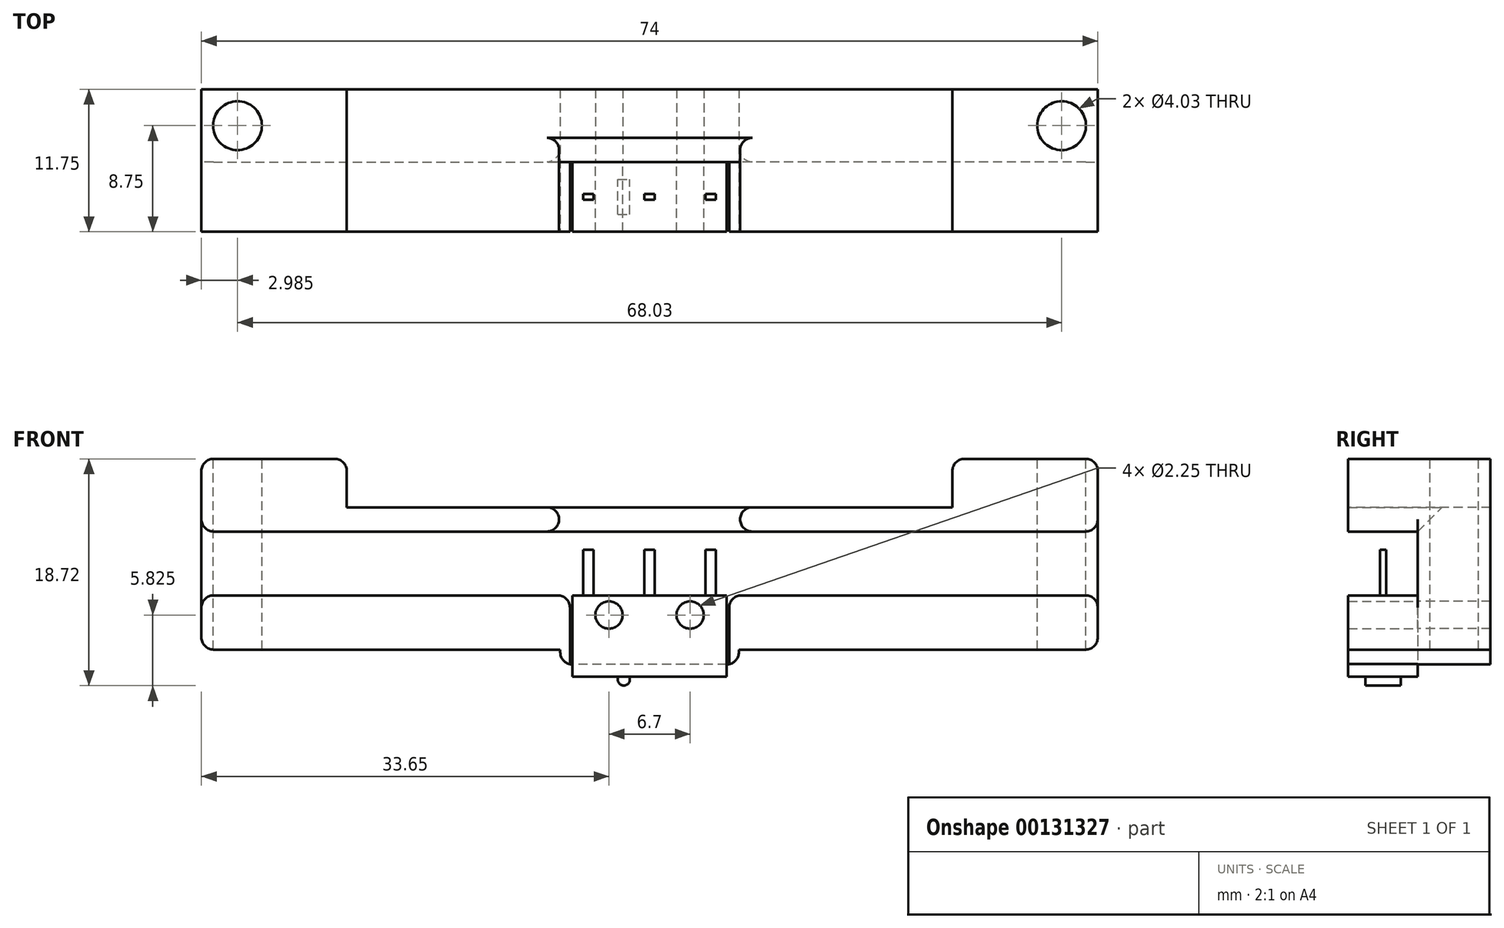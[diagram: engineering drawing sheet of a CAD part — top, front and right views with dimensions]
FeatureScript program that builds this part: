
annotation { "Feature Type Name" : "Feature", "Feature Type Description" : "" }
export const myFeature = defineFeature(function(context is Context, id is Id, definition is map)
    precondition{}
    {
        {
            assignVariable(context, id + "F0", {"name" : "MSDepth", "anyValue" : 5.75});
        }
        {
            assignVariable(context, id + "F1", {"name" : "PlungerH", "anyValue" : 0.75});
        }
        {
            assignVariable(context, id + "F2", {"name" : "PinH", "anyValue" : 3.75});
        }
        {
            var Q0;
            Q0=qCreatedBy(makeId("Front.planeOp"),FACE);
            var sketch = newSketch(context, id + "F3", { "sketchPlane" : qUnion([Q0])});
            skLineSegment(sketch, "E0.bottom", {"start": v(-6.38, 6.7) * mm, "end": v(6.38, 6.7) * mm});
            skLineSegment(sketch, "E0.top", {"start": v(-6.38, 0) * mm, "end": v(6.38, 0) * mm});
            skLineSegment(sketch, "E0.left", {"start": v(-6.38, 6.7) * mm, "end": v(-6.38, 0) * mm});
            skLineSegment(sketch, "E0.right", {"start": v(6.38, 6.7) * mm, "end": v(6.38, 0) * mm});
            skCircle(sketch, "E1", {"center": v(-3.35, 5.07) * mm, "radius": 1.13 * mm});
            skCircle(sketch, "E2", {"center": v(3.35, 5.07) * mm, "radius": 1.13 * mm});
            skLineSegment(sketch, "E3", {"start": v(0, 6.7) * mm, "end": v(0, 0) * mm, "construction": true});
            skSolve(sketch);
        }
        {
            var Q0;
            Q0 = qSketchRegion(id + "F3", true);
            extrude(context, id + "F4", {"entities" : qUnion([Q0]), "depth" : (getVariable(context, 'MSDepth')) * mm});
        }
        {
            var Q0;
            Q0=makeQuery(id+"F4.opExtrude","SWEPT_FACE",FACE,{"disambiguationData":[OSD([sQuery(id+"F3.wireOp",EDGE,"E0.top")])]});
            var sketch = newSketch(context, id + "F5", { "sketchPlane" : qUnion([Q0])});
            skLineSegment(sketch, "E4.bottom", {"start": v(-2.63, 4.32) * mm, "end": v(-1.63, 4.32) * mm});
            skLineSegment(sketch, "E4.top", {"start": v(-2.63, 1.42) * mm, "end": v(-1.63, 1.42) * mm});
            skLineSegment(sketch, "E4.left", {"start": v(-2.63, 4.32) * mm, "end": v(-2.63, 1.42) * mm});
            skLineSegment(sketch, "E4.right", {"start": v(-1.63, 4.32) * mm, "end": v(-1.63, 1.42) * mm});
            skLineSegment(sketch, "E5", {"start": v(-6.38, 2.88) * mm, "end": v(6.38, 2.88) * mm, "construction": true});
            skLineSegment(sketch, "E6", {"start": v(-2.63, 2.87) * mm, "end": v(-1.63, 2.87) * mm, "construction": true});
            skSolve(sketch);
        }
        {
            var Q0;
            Q0 = qSketchRegion(id + "F5", true);
            extrude(context, id + "F6", {"entities" : qUnion([Q0]), "depth" : (getVariable(context, 'PlungerH')) * mm});
        }
        {
            var Q0;
            Q0=makeQuery(id+"F6.opExtrude","CAP_EDGE",EDGE,{"disambiguationData":[OSD([sQuery(id+"F5.wireOp",EDGE,"E4.left")])],"isStart":false});
            var Q1;
            Q1=makeQuery(id+"F6.opExtrude","CAP_EDGE",EDGE,{"disambiguationData":[OSD([sQuery(id+"F5.wireOp",EDGE,"E4.right")])],"isStart":false});
            fillet(context, id + "F7", {"entities" : qUnion([Q0, Q1]), "radius" : 0.5 * mm, "tangentPropagation" : true, "allowEdgeOverflow" : false});
        }
        {
            var Q0;
            Q0=makeQuery(id+"F4.opExtrude","SWEPT_FACE",FACE,{"disambiguationData":[OSD([sQuery(id+"F3.wireOp",EDGE,"E0.bottom")])]});
            var sketch = newSketch(context, id + "F8", { "sketchPlane" : qUnion([Q0])});
            skLineSegment(sketch, "E7", {"start": v(-6.38, -2.88) * mm, "end": v(6.38, -2.88) * mm, "construction": true});
            skLineSegment(sketch, "E8.bottom", {"start": v(-5.48, -2.63) * mm, "end": v(-4.63, -2.63) * mm});
            skLineSegment(sketch, "E8.top", {"start": v(-5.48, -3.12) * mm, "end": v(-4.63, -3.12) * mm});
            skLineSegment(sketch, "E8.left", {"start": v(-5.48, -2.63) * mm, "end": v(-5.48, -3.12) * mm});
            skLineSegment(sketch, "E8.right", {"start": v(-4.63, -2.63) * mm, "end": v(-4.63, -3.13) * mm});
            skLineSegment(sketch, "E9.bottom", {"start": v(-0.42, -2.63) * mm, "end": v(0.43, -2.63) * mm});
            skLineSegment(sketch, "E9.top", {"start": v(-0.42, -3.12) * mm, "end": v(0.43, -3.12) * mm});
            skLineSegment(sketch, "E9.left", {"start": v(-0.42, -2.63) * mm, "end": v(-0.42, -3.13) * mm});
            skLineSegment(sketch, "E9.right", {"start": v(0.42, -2.63) * mm, "end": v(0.43, -3.13) * mm});
            skLineSegment(sketch, "E10.bottom", {"start": v(4.63, -2.62) * mm, "end": v(5.48, -2.62) * mm});
            skLineSegment(sketch, "E10.top", {"start": v(4.63, -3.12) * mm, "end": v(5.48, -3.12) * mm});
            skLineSegment(sketch, "E10.left", {"start": v(4.63, -2.62) * mm, "end": v(4.63, -3.12) * mm});
            skLineSegment(sketch, "E10.right", {"start": v(5.48, -2.62) * mm, "end": v(5.48, -3.12) * mm});
            skSolve(sketch);
        }
        {
            var Q0;
            Q0 = qSketchRegion(id + "F8", true);
            extrude(context, id + "F9", {"entities" : qUnion([Q0]), "depth" : (getVariable(context, 'PinH')) * mm});
        }
        {
            var Q0;
            Q0=makeQuery(id+"F4.opExtrude","CAP_FACE",FACE,{"disambiguationData":[OSD([sQuery(id+"F3.wireOp",EDGE,"E0.bottom"),sQuery(id+"F3.wireOp",EDGE,"E0.top"),sQuery(id+"F3.wireOp",EDGE,"E0.left"),sQuery(id+"F3.wireOp",EDGE,"E0.right"),sQuery(id+"F3.wireOp",EDGE,"E1"),sQuery(id+"F3.wireOp",EDGE,"E2")])],"isStart":true});
            var sketch = newSketch(context, id + "F10", { "sketchPlane" : qUnion([Q0])});
            skLineSegment(sketch, "E11.bottom", {"start": v(-7.38, 1) * mm, "end": v(7.38, 1) * mm});
            skLineSegment(sketch, "E11.left", {"start": v(-7.38, 1) * mm, "end": v(-7.38, 2.22) * mm});
            skLineSegment(sketch, "E11.right", {"start": v(7.38, 1) * mm, "end": v(7.38, 2.22) * mm});
            skLineSegment(sketch, "E12", {"start": v(-7.38, 2.22) * mm, "end": v(-37, 2.22) * mm});
            skLineSegment(sketch, "E13", {"start": v(7.38, 2.22) * mm, "end": v(37, 2.22) * mm});
            skLineSegment(sketch, "E14", {"start": v(-37, 2.22) * mm, "end": v(-37, 13.97) * mm});
            skLineSegment(sketch, "E15", {"start": v(37, 2.22) * mm, "end": v(37, 13.97) * mm});
            skLineSegment(sketch, "E16", {"start": v(37, 13.97) * mm, "end": v(-37, 13.97) * mm});
            skLineSegment(sketch, "E17", {"start": v(0, 1) * mm, "end": v(0, 13.97) * mm, "construction": true});
            skSolve(sketch);
        }
        {
            var Q0;
            {var subQ1=sQuery(id+"F10.wireOp",EDGE,"E11.left");Q0=makeQuery(id+"F10.imprint","IMPRINT",FACE,{"disambiguationData":[TD([[makeQuery(id+"F10.imprint","IMPRINT",EDGE,{"derivedFrom":subQ1}),-1.0]])]});}
            var Q1;
            {var subQ0=makeQuery(id+"F4.opExtrude","CAP_EDGE",EDGE,{"disambiguationData":[OSD([sQuery(id+"F3.wireOp",EDGE,"E0.bottom")])],"isStart":true});Q1=makeQuery(id+"F10.imprint","IMPRINT",FACE,{"disambiguationData":[TD([[makeQuery(id+"F10.imprint","IMPRINT",EDGE,{"derivedFrom":subQ0}),1.0]])]});}
            extrude(context, id + "F11", {"entities" : qUnion([Q0, Q1]), "depth" : 6 * mm});
        }
        {
            var Q0;
            Q0=makeQuery(id+"F11.opExtrude","SWEPT_FACE",FACE,{"disambiguationData":[OSD([sQuery(id+"F10.wireOp",EDGE,"E16")])]});
            var sketch = newSketch(context, id + "F12", { "sketchPlane" : qUnion([Q0])});
            skLineSegment(sketch, "E18", {"start": v(-37, 3) * mm, "end": v(37, 3) * mm, "construction": true});
            skCircle(sketch, "E19", {"center": v(-34.02, 3) * mm, "radius": 2.02 * mm});
            skCircle(sketch, "E20", {"center": v(34.02, 3) * mm, "radius": 2.02 * mm});
            skLineSegment(sketch, "E21", {"start": v(0, 6) * mm, "end": v(0, 0) * mm, "construction": true});
            skSolve(sketch);
        }
        {
            var Q0;
            Q0 = qSketchRegion(id + "F12", true);
            var Q1;
            Q1=makeQuery(id+"F11.opExtrude","SWEPT_FACE",FACE,{"disambiguationData":[OSD([sQuery(id+"F10.wireOp",EDGE,"E13")])]});
            extrude(context, id + "F13", {"entities" : qUnion([Q0]), "operationType" : NewBodyOperationType.REMOVE, "endBound" : BoundingType.UP_TO_SURFACE, "oppositeDirection" : true, "endBoundEntityFace" : qUnion([Q1]), "depth" : 25 * mm});
        }
        {
            var Q0;
            Q0=makeQuery(id+"F11.opExtrude","CAP_FACE",FACE,{"disambiguationData":[OSD([sQuery(id+"F3.wireOp",EDGE,"E1"),sQuery(id+"F3.wireOp",EDGE,"E2"),sQuery(id+"F10.wireOp",EDGE,"E11.bottom"),sQuery(id+"F10.wireOp",EDGE,"E11.left"),sQuery(id+"F10.wireOp",EDGE,"E11.right"),sQuery(id+"F10.wireOp",EDGE,"E12"),sQuery(id+"F10.wireOp",EDGE,"E13"),sQuery(id+"F10.wireOp",EDGE,"E14"),sQuery(id+"F10.wireOp",EDGE,"E15"),sQuery(id+"F10.wireOp",EDGE,"E16")])],"isStart":true});
            var sketch = newSketch(context, id + "F14", { "sketchPlane" : qUnion([Q0])});
            skLineSegment(sketch, "E22", {"start": v(-8.57, 6.7) * mm, "end": v(-6.58, 6.7) * mm});
            skLineSegment(sketch, "E23", {"start": v(-6.58, 6.7) * mm, "end": v(-6.58, 1) * mm});
            skLineSegment(sketch, "E24", {"start": v(0, 13.97) * mm, "end": v(0, -6.79) * mm, "construction": true});
            skLineSegment(sketch, "E25.MirrorCS", {"start": v(6.57, 6.7) * mm, "end": v(6.57, 1) * mm});
            skLineSegment(sketch, "E26.MirrorCS", {"start": v(8.57, 6.7) * mm, "end": v(6.57, 6.7) * mm});
            skLineSegment(sketch, "E27", {"start": v(8.57, 6.7) * mm, "end": v(37, 6.7) * mm});
            skLineSegment(sketch, "E28", {"start": v(37, 11.97) * mm, "end": v(7.48, 11.97) * mm});
            skLineSegment(sketch, "E29", {"start": v(7.48, 11.97) * mm, "end": v(7.48, 13.97) * mm});
            skLineSegment(sketch, "E30.MirrorCS", {"start": v(-8.58, 6.7) * mm, "end": v(-37, 6.7) * mm});
            skLineSegment(sketch, "E31.MirrorCS", {"start": v(-37, 11.97) * mm, "end": v(-7.48, 11.97) * mm});
            skLineSegment(sketch, "E32.MirrorCS", {"start": v(-7.48, 11.97) * mm, "end": v(-7.48, 13.97) * mm});
            skSolve(sketch);
        }
        {
            var Q0;
            Q0=makeQuery(id+"F14.imprint","IMPRINT",FACE,{"disambiguationData":[TD([[makeQuery(id+"F14.imprint","IMPRINT",EDGE,{"derivedFrom":sQuery(id+"F14.wireOp",EDGE,"E22")}),-1.0]])]});
            var Q1;
            {var subQ4=sQuery(id+"F14.wireOp",EDGE,"E25.MirrorCS");Q1=makeQuery(id+"F14.imprint","IMPRINT",FACE,{"disambiguationData":[TD([[makeQuery(id+"F14.imprint","IMPRINT",EDGE,{"derivedFrom":subQ4}),1.0]])]});}
            var Q2;
            {var subQ0=sQuery(id+"F14.wireOp",EDGE,"E28");Q2=makeQuery(id+"F14.imprint","IMPRINT",FACE,{"disambiguationData":[TD([[makeQuery(id+"F14.imprint","IMPRINT",EDGE,{"derivedFrom":subQ0}),-1.0]])]});}
            var Q3;
            {var subQ0=sQuery(id+"F14.wireOp",EDGE,"E31.MirrorCS");Q3=makeQuery(id+"F14.imprint","IMPRINT",FACE,{"disambiguationData":[TD([[makeQuery(id+"F14.imprint","IMPRINT",EDGE,{"derivedFrom":subQ0}),1.0]])]});}
            var Q4;
            Q4=makeQuery(id+"F4.opExtrude","CAP_FACE",FACE,{"disambiguationData":[OSD([sQuery(id+"F3.wireOp",EDGE,"E0.bottom"),sQuery(id+"F3.wireOp",EDGE,"E0.top"),sQuery(id+"F3.wireOp",EDGE,"E0.left"),sQuery(id+"F3.wireOp",EDGE,"E0.right"),sQuery(id+"F3.wireOp",EDGE,"E1"),sQuery(id+"F3.wireOp",EDGE,"E2")])],"isStart":false});
            extrude(context, id + "F15", {"entities" : qUnion([Q0, Q1, Q2, Q3]), "operationType" : NewBodyOperationType.ADD, "endBound" : BoundingType.UP_TO_SURFACE, "endBoundEntityFace" : qUnion([Q4]), "depth" : 25 * mm});
        }
        {
            var Q0;
            {var subQ0=sQuery(id+"F10.wireOp",EDGE,"E16");var subQ1=makeQuery(id+"F11.opExtrude","CAP_EDGE",EDGE,{"disambiguationData":[OSD([subQ0])],"isStart":true});Q0=makeQuery(id+"F15.boolean.opBoolean","MERGE",FACE,{"derivedFrom":[makeQuery(id+"F11.opExtrude","SWEPT_FACE",FACE,{"disambiguationData":[OSD([subQ0])]}),makeQuery(id+"F15.opExtrude","SWEPT_FACE",FACE,{"disambiguationData":[OSD([subQ0]),TDD([makeQuery(id+"F14.imprint","IMPRINT",EDGE,{"disambiguationData":[TD([[makeQuery(id+"F14.imprint","INTERSECT",VERTEX,{"derivedFrom":[makeQuery(id+"F11.opExtrude","CAP_EDGE",EDGE,{"disambiguationData":[OSD([sQuery(id+"F10.wireOp",EDGE,"E14")])],"isStart":true}),subQ1]}),1.0]])],"derivedFrom":subQ1})])]}),makeQuery(id+"F15.opExtrude","SWEPT_FACE",FACE,{"disambiguationData":[OSD([subQ0]),TDD([makeQuery(id+"F14.imprint","IMPRINT",EDGE,{"disambiguationData":[TD([[makeQuery(id+"F14.imprint","INTERSECT",VERTEX,{"derivedFrom":[makeQuery(id+"F11.opExtrude","CAP_EDGE",EDGE,{"disambiguationData":[OSD([sQuery(id+"F10.wireOp",EDGE,"E15")])],"isStart":true}),subQ1]}),-1.0]])],"derivedFrom":subQ1})])]})]});}
            var sketch = newSketch(context, id + "F16", { "sketchPlane" : qUnion([Q0])});
            skLineSegment(sketch, "E33", {"start": v(-25, 6) * mm, "end": v(-25, -5.75) * mm});
            skLineSegment(sketch, "E34", {"start": v(25, 6) * mm, "end": v(25, -5.75) * mm});
            skSolve(sketch);
        }
        {
            var Q0;
            {var subQ4=sQuery(id+"F16.wireOp",EDGE,"E34");Q0=makeQuery(id+"F16.imprint","IMPRINT",FACE,{"disambiguationData":[TD([[makeQuery(id+"F16.imprint","IMPRINT",EDGE,{"derivedFrom":subQ4}),1.0]])]});}
            var Q1;
            {var subQ4=sQuery(id+"F16.wireOp",EDGE,"E33");Q1=makeQuery(id+"F16.imprint","IMPRINT",FACE,{"disambiguationData":[TD([[makeQuery(id+"F16.imprint","IMPRINT",EDGE,{"derivedFrom":subQ4}),-1.0]])]});}
            extrude(context, id + "F17", {"entities" : qUnion([Q0, Q1]), "operationType" : NewBodyOperationType.ADD, "depth" : 4 * mm});
        }
        {
            var Q0;
            Q0=makeQuery(id+"F15.opExtrude","SWEPT_EDGE",EDGE,{"disambiguationData":[OSD([sQuery(id+"F10.wireOp",EDGE,"E15"),sQuery(id+"F14.wireOp",EDGE,"E31.MirrorCS")])]});
            var Q1;
            Q1=makeQuery(id+"F15.opExtrude","SWEPT_EDGE",EDGE,{"disambiguationData":[OSD([sQuery(id+"F10.wireOp",EDGE,"E15"),sQuery(id+"F14.wireOp",EDGE,"E30.MirrorCS")])]});
            var Q2;
            {var subQ0=sQuery(id+"F10.wireOp",EDGE,"E16");var subQ1=sQuery(id+"F10.wireOp",EDGE,"E15");Q2=makeQuery(id+"F15.boolean.opBoolean","MERGE",EDGE,{"derivedFrom":[makeQuery(id+"F11.opExtrude","SWEPT_EDGE",EDGE,{"disambiguationData":[OSD([subQ1,subQ0])]}),makeQuery(id+"F15.opExtrude","SWEPT_EDGE",EDGE,{"disambiguationData":[OSD([subQ1,subQ0])]})]});}
            var Q3;
            {var subQ0=sQuery(id+"F10.wireOp",EDGE,"E15");var subQ1=sQuery(id+"F10.wireOp",EDGE,"E13");Q3=makeQuery(id+"F15.boolean.opBoolean","MERGE",EDGE,{"derivedFrom":[makeQuery(id+"F11.opExtrude","SWEPT_EDGE",EDGE,{"disambiguationData":[OSD([subQ1,subQ0])]}),makeQuery(id+"F15.opExtrude","SWEPT_EDGE",EDGE,{"disambiguationData":[OSD([subQ1,subQ0])]})]});}
            var Q4;
            {var subQ0=sQuery(id+"F10.wireOp",EDGE,"E14");var subQ1=sQuery(id+"F10.wireOp",EDGE,"E12");Q4=makeQuery(id+"F15.boolean.opBoolean","MERGE",EDGE,{"derivedFrom":[makeQuery(id+"F11.opExtrude","SWEPT_EDGE",EDGE,{"disambiguationData":[OSD([subQ1,subQ0])]}),makeQuery(id+"F15.opExtrude","SWEPT_EDGE",EDGE,{"disambiguationData":[OSD([subQ1,subQ0])]})]});}
            var Q5;
            Q5=makeQuery(id+"F15.opExtrude","SWEPT_EDGE",EDGE,{"disambiguationData":[OSD([sQuery(id+"F10.wireOp",EDGE,"E14"),sQuery(id+"F14.wireOp",EDGE,"E27")])]});
            var Q6;
            Q6=makeQuery(id+"F15.opExtrude","SWEPT_EDGE",EDGE,{"disambiguationData":[OSD([sQuery(id+"F10.wireOp",EDGE,"E14"),sQuery(id+"F14.wireOp",EDGE,"E28")])]});
            var Q7;
            {var subQ0=sQuery(id+"F10.wireOp",EDGE,"E16");var subQ1=sQuery(id+"F10.wireOp",EDGE,"E14");Q7=makeQuery(id+"F15.boolean.opBoolean","MERGE",EDGE,{"derivedFrom":[makeQuery(id+"F11.opExtrude","SWEPT_EDGE",EDGE,{"disambiguationData":[OSD([subQ1,subQ0])]}),makeQuery(id+"F15.opExtrude","SWEPT_EDGE",EDGE,{"disambiguationData":[OSD([subQ1,subQ0])]})]});}
            var Q8;
            {var subQ0=sQuery(id+"F10.wireOp",EDGE,"E11.right");var subQ1=sQuery(id+"F10.wireOp",EDGE,"E11.bottom");Q8=makeQuery(id+"F15.boolean.opBoolean","MERGE",EDGE,{"derivedFrom":[makeQuery(id+"F11.opExtrude","SWEPT_EDGE",EDGE,{"disambiguationData":[OSD([subQ1,subQ0])]}),makeQuery(id+"F15.opExtrude","SWEPT_EDGE",EDGE,{"disambiguationData":[OSD([subQ1,subQ0])]})]});}
            var Q9;
            {var subQ0=sQuery(id+"F10.wireOp",EDGE,"E11.left");var subQ1=sQuery(id+"F10.wireOp",EDGE,"E11.bottom");Q9=makeQuery(id+"F15.boolean.opBoolean","MERGE",EDGE,{"derivedFrom":[makeQuery(id+"F11.opExtrude","SWEPT_EDGE",EDGE,{"disambiguationData":[OSD([subQ1,subQ0])]}),makeQuery(id+"F15.opExtrude","SWEPT_EDGE",EDGE,{"disambiguationData":[OSD([subQ1,subQ0])]})]});}
            var Q10;
            Q10=makeQuery(id+"F15.opExtrude","SWEPT_EDGE",EDGE,{"disambiguationData":[OSD([sQuery(id+"F14.wireOp",EDGE,"E22"),sQuery(id+"F14.wireOp",EDGE,"E23")])]});
            var Q11;
            Q11=makeQuery(id+"F15.opExtrude","SWEPT_EDGE",EDGE,{"disambiguationData":[OSD([sQuery(id+"F14.wireOp",EDGE,"E31.MirrorCS"),sQuery(id+"F14.wireOp",EDGE,"E32.MirrorCS")])]});
            var Q12;
            Q12=makeQuery(id+"F15.opExtrude","SWEPT_EDGE",EDGE,{"disambiguationData":[OSD([sQuery(id+"F10.wireOp",EDGE,"E16"),sQuery(id+"F14.wireOp",EDGE,"E32.MirrorCS")])]});
            var Q13;
            Q13=makeQuery(id+"F15.opExtrude","SWEPT_EDGE",EDGE,{"disambiguationData":[OSD([sQuery(id+"F10.wireOp",EDGE,"E16"),sQuery(id+"F14.wireOp",EDGE,"E29")])]});
            var Q14;
            Q14=makeQuery(id+"F15.opExtrude","SWEPT_EDGE",EDGE,{"disambiguationData":[OSD([sQuery(id+"F14.wireOp",EDGE,"E28"),sQuery(id+"F14.wireOp",EDGE,"E29")])]});
            var Q15;
            Q15=makeQuery(id+"F15.opExtrude","SWEPT_EDGE",EDGE,{"disambiguationData":[OSD([sQuery(id+"F14.wireOp",EDGE,"E25.MirrorCS"),sQuery(id+"F14.wireOp",EDGE,"E26.MirrorCS")])]});
            var Q16;
            Q16=makeQuery(id+"F17.opExtrude","CAP_EDGE",EDGE,{"disambiguationData":[OSD([sQuery(id+"F10.wireOp",EDGE,"E15"),sQuery(id+"F10.wireOp",EDGE,"E16")])],"isStart":false});
            var Q17;
            Q17=makeQuery(id+"F17.opExtrude","CAP_EDGE",EDGE,{"disambiguationData":[OSD([sQuery(id+"F16.wireOp",EDGE,"E33")])],"isStart":false});
            var Q18;
            Q18=makeQuery(id+"F17.opExtrude","CAP_EDGE",EDGE,{"disambiguationData":[OSD([sQuery(id+"F16.wireOp",EDGE,"E34")])],"isStart":false});
            var Q19;
            Q19=makeQuery(id+"F17.opExtrude","CAP_EDGE",EDGE,{"disambiguationData":[OSD([sQuery(id+"F10.wireOp",EDGE,"E14"),sQuery(id+"F10.wireOp",EDGE,"E16")])],"isStart":false});
            var Q20;
            Q20=makeQuery(id+"F17.opExtrude","CAP_EDGE",EDGE,{"disambiguationData":[OSD([sQuery(id+"F16.wireOp",EDGE,"E33")])],"isStart":true});
            var Q21;
            Q21=makeQuery(id+"F17.opExtrude","CAP_EDGE",EDGE,{"disambiguationData":[OSD([sQuery(id+"F16.wireOp",EDGE,"E34")])],"isStart":true});
            fillet(context, id + "F18", {"entities" : qUnion([Q0, Q1, Q2, Q3, Q4, Q5, Q6, Q7, Q8, Q9, Q10, Q11, Q12, Q13, Q14, Q15, Q16, Q17, Q18, Q19, Q20, Q21]), "radius" : 1 * mm, "tangentPropagation" : true, "allowEdgeOverflow" : false});
        }
        {
            var Q0;
            Q0=makeQuery(id+"F11.opExtrude","CAP_EDGE",EDGE,{"disambiguationData":[OSD([sQuery(id+"F10.wireOp",EDGE,"E16")])],"isStart":true});
            chamfer(context, id + "F19", {"entities" : qUnion([Q0]), "width" : 2 * mm});
        }
    });
